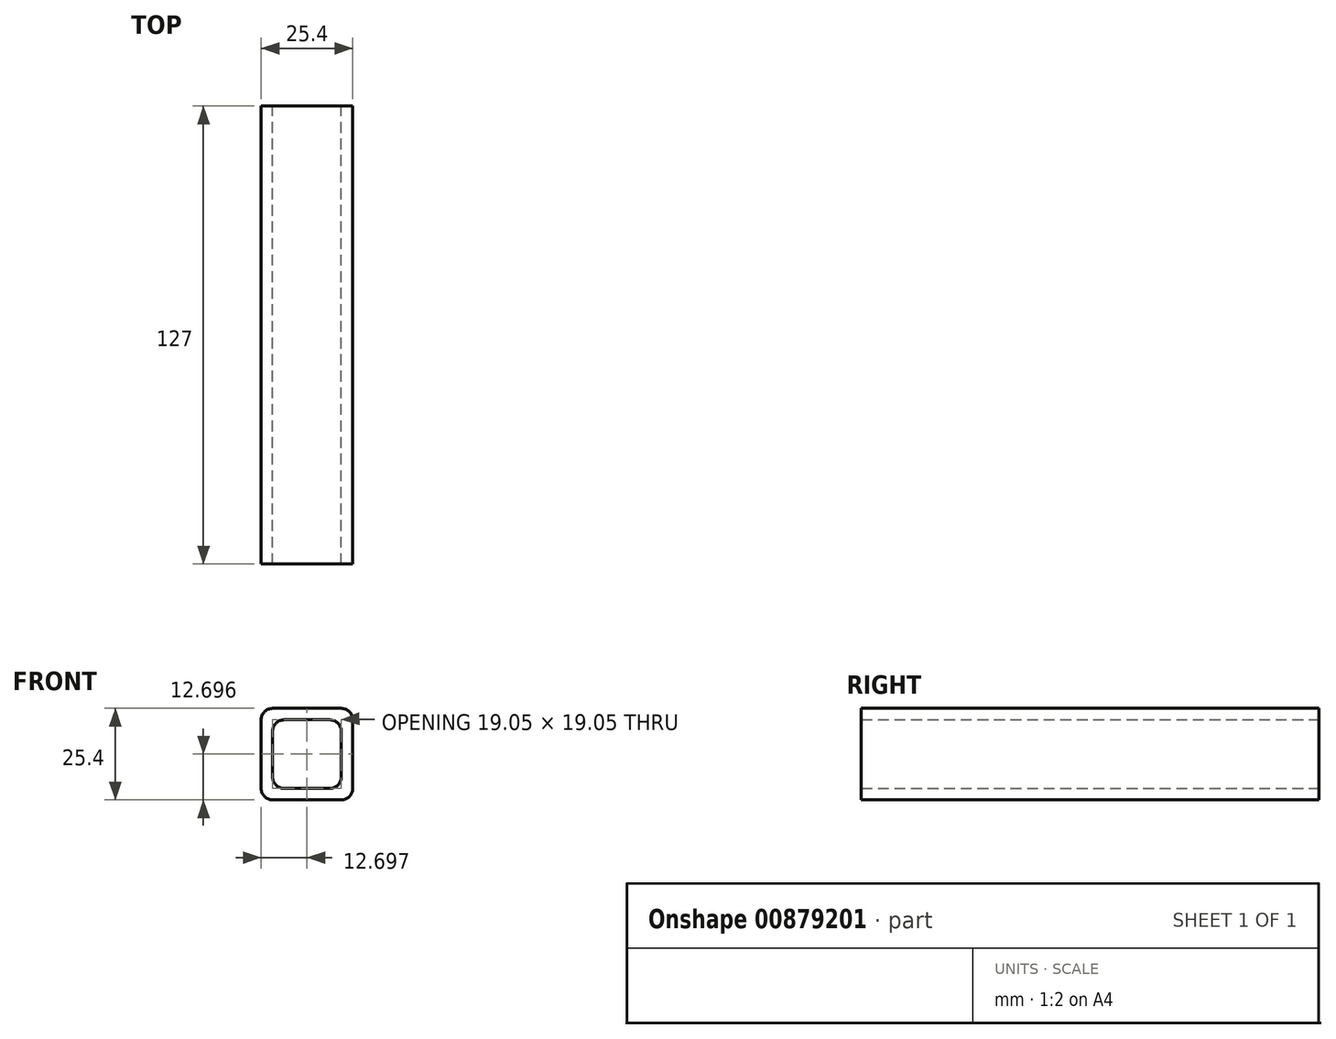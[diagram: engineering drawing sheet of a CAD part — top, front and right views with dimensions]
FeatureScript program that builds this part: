
annotation { "Feature Type Name" : "Feature", "Feature Type Description" : "" }
export const myFeature = defineFeature(function(context is Context, id is Id, definition is map)
    precondition{}
    {
        {
            var Q0;
            Q0=qCreatedBy(makeId("Front.planeOp"),FACE);
            var sketch = newSketch(context, id + "F0", { "sketchPlane" : qUnion([Q0])});
            skLineSegment(sketch, "E0.bottom", {"start": v(9.13, -13) * mm, "end": v(-9.92, -13) * mm});
            skLineSegment(sketch, "E0.top", {"start": v(9.13, 12.4) * mm, "end": v(-9.92, 12.4) * mm});
            skLineSegment(sketch, "E0.left", {"start": v(12.3, -9.82) * mm, "end": v(12.3, 9.23) * mm});
            skLineSegment(sketch, "E0.right", {"start": v(-13.1, -9.82) * mm, "end": v(-13.1, 9.23) * mm});
            skLineSegment(sketch, "E1.bottom", {"start": v(5.96, -9.82) * mm, "end": v(-6.74, -9.82) * mm});
            skLineSegment(sketch, "E1.top", {"start": v(5.96, 9.23) * mm, "end": v(-6.74, 9.23) * mm});
            skLineSegment(sketch, "E1.left", {"start": v(9.13, -6.64) * mm, "end": v(9.13, 6.06) * mm});
            skLineSegment(sketch, "E1.right", {"start": v(-9.92, -6.64) * mm, "end": v(-9.92, 6.06) * mm});
            skPoint(sketch, "E2.visualSharp", {"position": v(9.13, 9.23) * mm});
            skArc(sketch, "E2.filletArc", {"start": v(9.13, 6.06) * mm, "mid": v(8.2, 8.3) * mm, "end": v(5.96, 9.23) * mm});
            skPoint(sketch, "E3.visualSharp", {"position": v(-9.92, 9.23) * mm});
            skArc(sketch, "E3.filletArc", {"start": v(-6.74, 9.23) * mm, "mid": v(-8.99, 8.3) * mm, "end": v(-9.92, 6.06) * mm});
            skPoint(sketch, "E4.visualSharp", {"position": v(-9.92, -9.82) * mm});
            skArc(sketch, "E4.filletArc", {"start": v(-9.92, -6.64) * mm, "mid": v(-8.99, -8.89) * mm, "end": v(-6.74, -9.82) * mm});
            skPoint(sketch, "E5.visualSharp", {"position": v(9.13, -9.82) * mm});
            skArc(sketch, "E5.filletArc", {"start": v(5.96, -9.82) * mm, "mid": v(8.2, -8.89) * mm, "end": v(9.13, -6.64) * mm});
            skPoint(sketch, "E6.visualSharp", {"position": v(12.3, 12.4) * mm});
            skArc(sketch, "E6.filletArc", {"start": v(12.3, 9.23) * mm, "mid": v(11.38, 11.48) * mm, "end": v(9.13, 12.4) * mm});
            skPoint(sketch, "E7.visualSharp", {"position": v(-13.1, 12.4) * mm});
            skArc(sketch, "E7.filletArc", {"start": v(-9.92, 12.4) * mm, "mid": v(-12.16, 11.48) * mm, "end": v(-13.1, 9.23) * mm});
            skPoint(sketch, "E8.visualSharp", {"position": v(-13.1, -13) * mm});
            skArc(sketch, "E8.filletArc", {"start": v(-13.1, -9.82) * mm, "mid": v(-12.16, -12.06) * mm, "end": v(-9.92, -13) * mm});
            skPoint(sketch, "E9.visualSharp", {"position": v(12.3, -13) * mm});
            skArc(sketch, "E9.filletArc", {"start": v(9.13, -13) * mm, "mid": v(11.38, -12.06) * mm, "end": v(12.3, -9.82) * mm});
            skSolve(sketch);
        }
        {
            var Q0;
            Q0=qSketchRegion(id+"F0",true);
            extrude(context, id + "F1", {"entities" : qUnion([Q0]), "depth" : 127 * mm, "offsetDistance" : 25.4 * mm});
        }
    });
